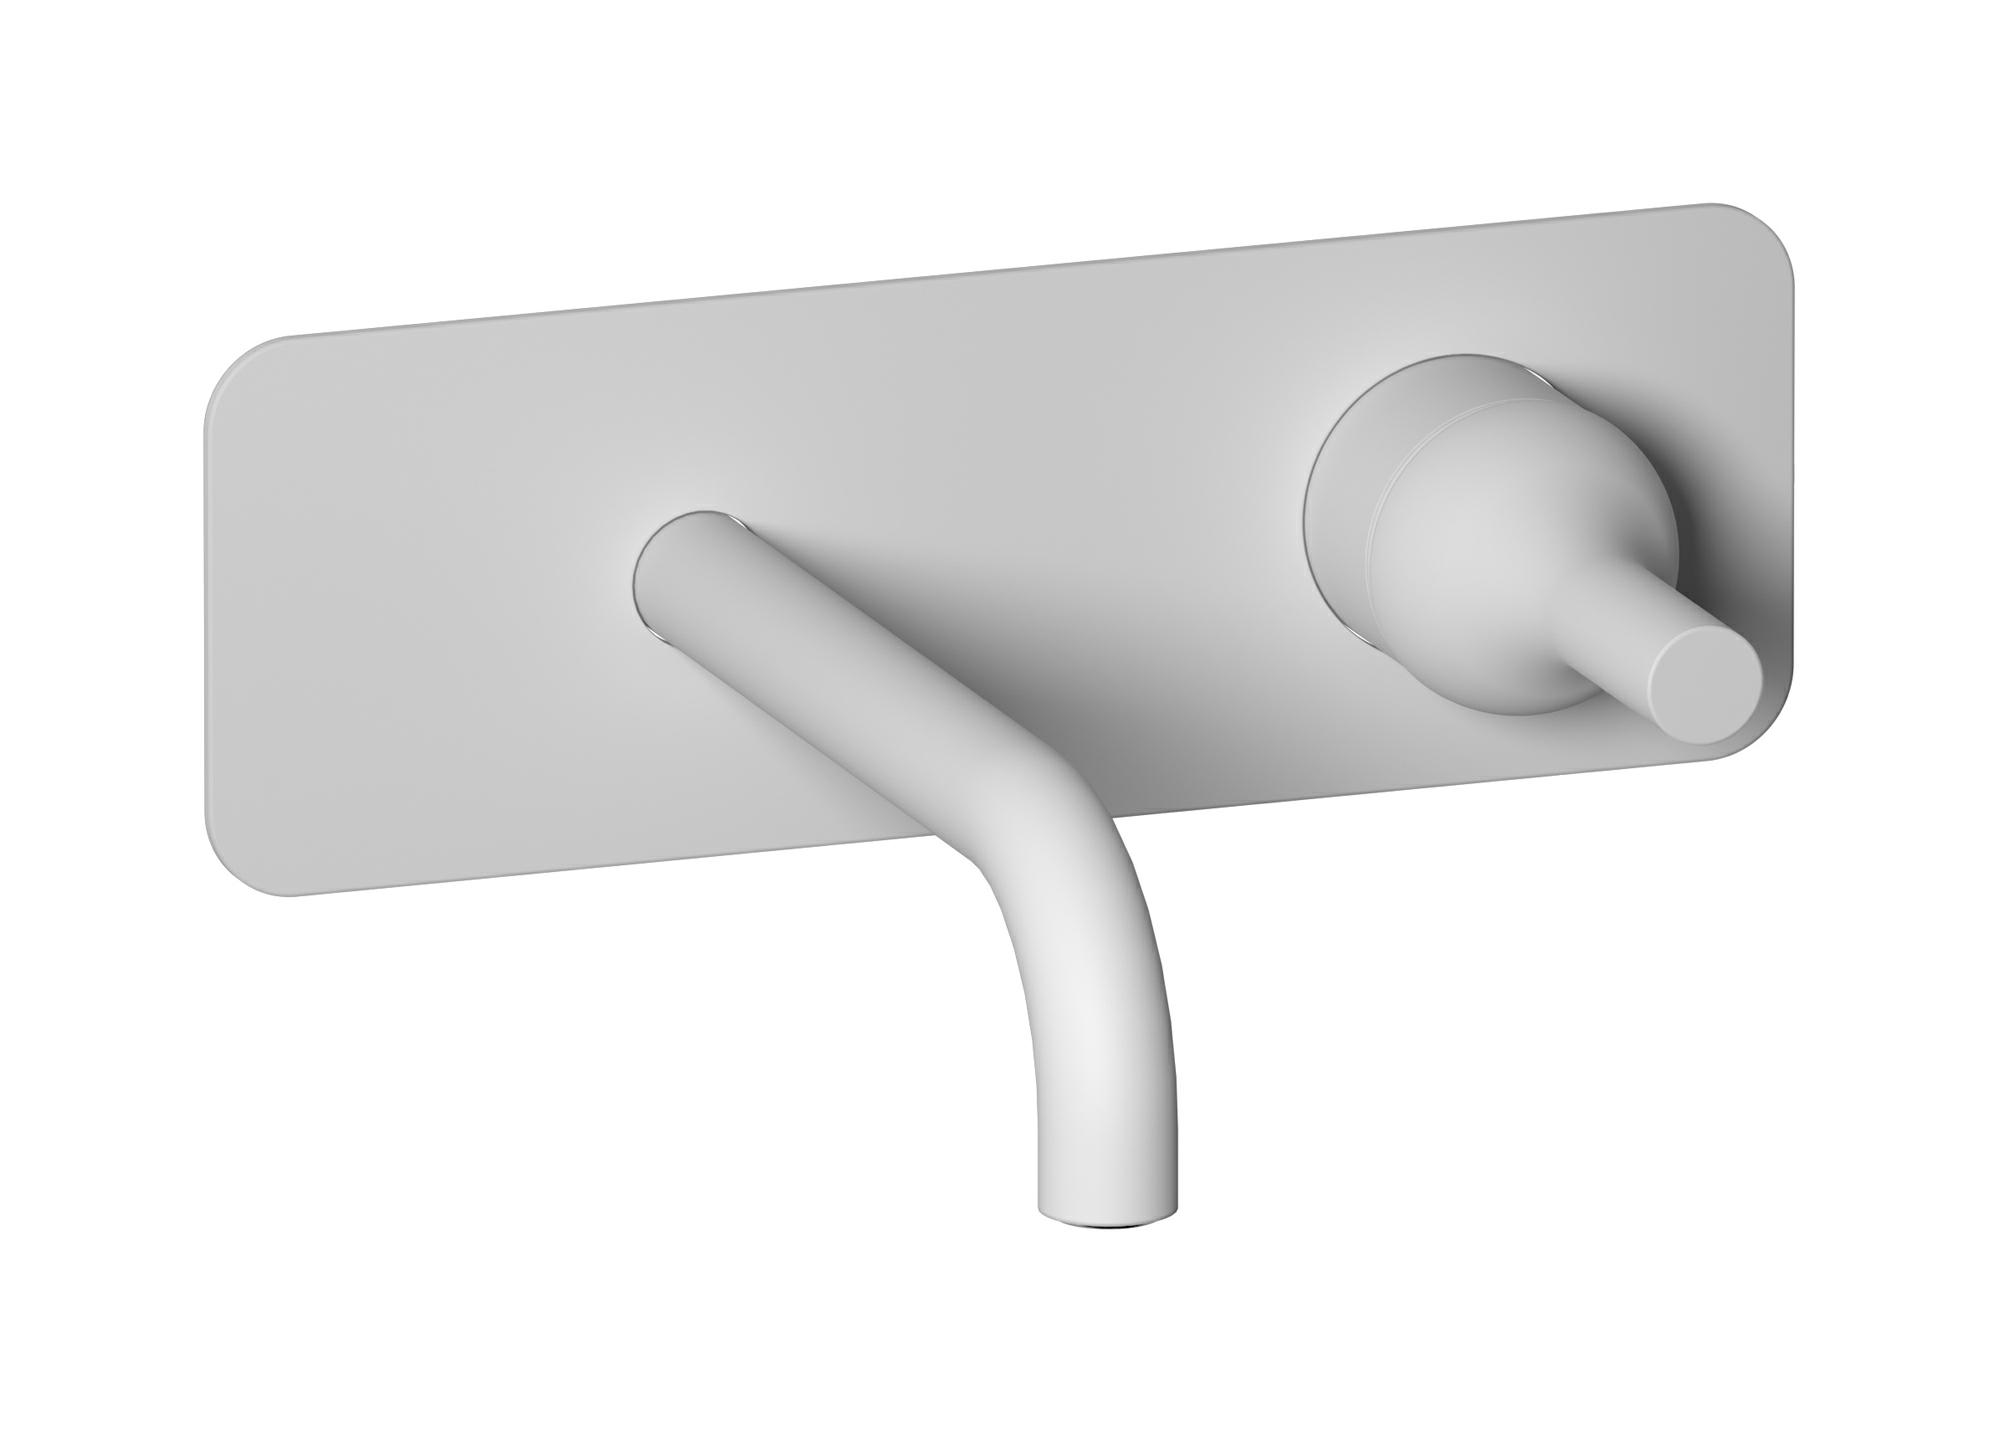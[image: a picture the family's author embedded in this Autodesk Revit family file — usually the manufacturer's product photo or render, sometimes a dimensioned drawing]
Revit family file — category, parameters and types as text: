
# Revit family: BI206
name_source: partatom
category: Apparecchi idraulici
units: mm (PartAtom-declared; Revit-internal decimal feet)

## family parameters
Basato su piano di lavoro = No
Condiviso = No
Mantieni orientamento annotazione = No
Numero OmniClass = 23.45.55.17
Punto di calcolo locali = No
Quota connettore circolare = Usa diametro
Sempre verticale = Sì
Taglio con vuoti quando caricato = No
Tipo di parte = Normale
Titolo OmniClass = Mixing Faucets

## types (4) — shared parameters
Cold water inlet = 10 mm  [stored 0.0328084 ft]
Commenti sul tipo = Wall mounted washbasin mixer complete with drain
Connessione CW = No
Connessione HW = No
Connessione di scarico = No
Connessione di ventilazione = No
Descrizione = Wall mounted washbasin mixer complete with drain
Hot water inlet = 10 mm  [stored 0.0328084 ft]
Produttore = IB Rubinetterie S.p.A.
URL = https://www.weareib.it
zero-valued in all types: Prospetto di default

## per-type parameters (varying)
| type | Finishes surface | Immagine tipo | Modello |
| Chrome | IB_Chrome | BI206CC.jpg | BI206CC |
| Matt White | IB_matt white | BI206BO.jpg | BI206BO |
| Matt Black | IB_matt black | BI206NP.jpg | BI206NP |
| Brushed Nickel | IB_Brushed nickel | BI206SS.jpg | BI206SS |

note: [stored X ft] marks values corroborated as IEEE doubles in the binary element streams (Revit-internal decimal feet)
